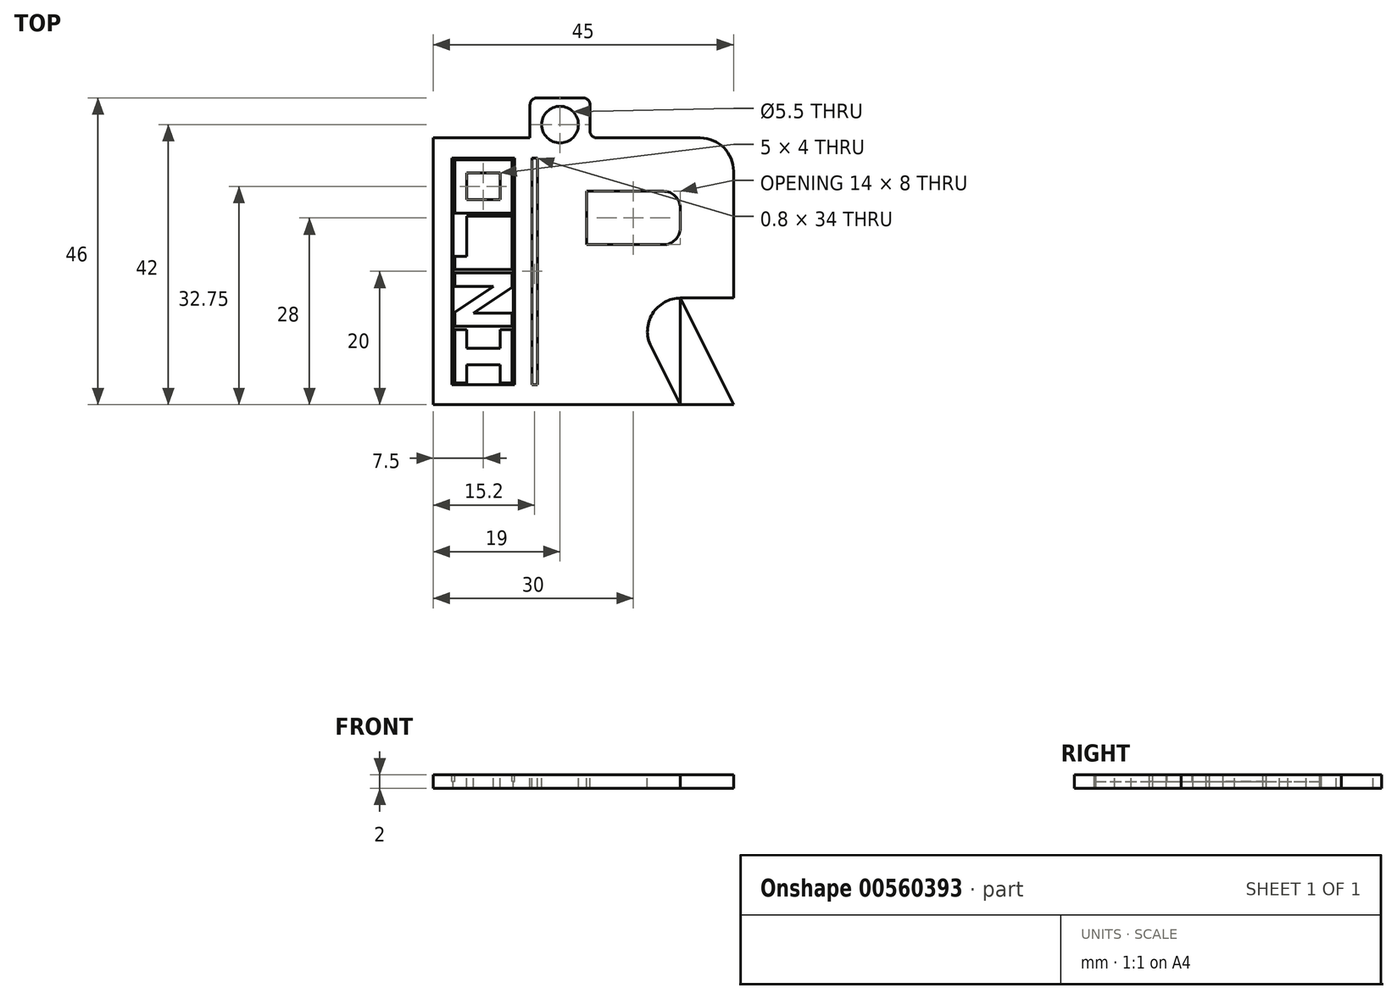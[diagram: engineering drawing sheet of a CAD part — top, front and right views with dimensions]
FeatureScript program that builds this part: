
annotation { "Feature Type Name" : "Feature", "Feature Type Description" : "" }
export const myFeature = defineFeature(function(context is Context, id is Id, definition is map)
    precondition{}
    {
        {
            var Q0;
            Q0=qCreatedBy(makeId("Top.planeOp"),FACE);
            var sketch = newSketch(context, id + "F0", { "sketchPlane" : qUnion([Q0])});
            skPoint(sketch, "E0.middle", {"position": v(0, 0) * mm});
            skLineSegment(sketch, "E1.bottom", {"start": v(-15, 20) * mm, "end": v(15, 20) * mm});
            skLineSegment(sketch, "E1.top", {"start": v(-15, -20) * mm, "end": v(15, -20) * mm});
            skLineSegment(sketch, "E1.left", {"start": v(-15, 20) * mm, "end": v(-15, -20) * mm});
            skLineSegment(sketch, "E1.right", {"start": v(15, 20) * mm, "end": v(15, -20) * mm});
            skSolve(sketch);
        }
        {
            var Q0;
            Q0=makeQuery(id+"F0.imprint","IMPRINT",FACE,{"disambiguationData":[TD([[makeQuery(id+"F0.imprint","IMPRINT",EDGE,{"derivedFrom":sQuery(id+"F0.wireOp",EDGE,"E1.bottom")}),-1.0]])]});
            extrude(context, id + "F1", {"entities" : qUnion([Q0]), "depth" : 2 * mm, "offsetDistance" : 25 * mm});
        }
        {
            var Q0;
            Q0=makeQuery(id+"F1.opExtrude","CAP_FACE",FACE,{"disambiguationData":[OSD([sQuery(id+"F0.wireOp",EDGE,"E1.bottom"),sQuery(id+"F0.wireOp",EDGE,"E1.top"),sQuery(id+"F0.wireOp",EDGE,"E1.left"),sQuery(id+"F0.wireOp",EDGE,"E1.right")])],"isStart":false});
            var sketch = newSketch(context, id + "F2", { "sketchPlane" : qUnion([Q0])});
            skLineSegment(sketch, "E2.bottom", {"start": v(-7, 12) * mm, "end": v(7, 12) * mm});
            skLineSegment(sketch, "E2.top", {"start": v(-7, 4) * mm, "end": v(7, 4) * mm});
            skLineSegment(sketch, "E2.left", {"start": v(-7, 12) * mm, "end": v(-7, 4) * mm});
            skLineSegment(sketch, "E2.right", {"start": v(7, 12) * mm, "end": v(7, 4) * mm});
            skSolve(sketch);
        }
        {
            var Q0;
            Q0=makeQuery(id+"F2.imprint","IMPRINT",FACE,{"disambiguationData":[TD([[makeQuery(id+"F2.imprint","IMPRINT",EDGE,{"derivedFrom":sQuery(id+"F2.wireOp",EDGE,"E2.bottom")}),-1.0]])]});
            extrude(context, id + "F3", {"entities" : qUnion([Q0]), "operationType" : NewBodyOperationType.REMOVE, "oppositeDirection" : true, "depth" : 10 * mm, "offsetDistance" : 25 * mm});
        }
        {
            var Q0;
            Q0=makeQuery(id+"F1.opExtrude","CAP_FACE",FACE,{"disambiguationData":[OSD([sQuery(id+"F0.wireOp",EDGE,"E1.bottom"),sQuery(id+"F0.wireOp",EDGE,"E1.top"),sQuery(id+"F0.wireOp",EDGE,"E1.left"),sQuery(id+"F0.wireOp",EDGE,"E1.right")])],"isStart":false});
            var sketch = newSketch(context, id + "F4", { "sketchPlane" : qUnion([Q0])});
            skLineSegment(sketch, "E3.bottom", {"start": v(-7, -4) * mm, "end": v(7, -4) * mm});
            skLineSegment(sketch, "E3.top", {"start": v(-7, -20) * mm, "end": v(7, -20) * mm});
            skLineSegment(sketch, "E3.left", {"start": v(-7, -4) * mm, "end": v(-7, -20) * mm});
            skLineSegment(sketch, "E3.right", {"start": v(7, -4) * mm, "end": v(7, -20) * mm});
            skLineSegment(sketch, "E4", {"start": v(-1, -4) * mm, "end": v(7, -20) * mm});
            skLineSegment(sketch, "E5", {"start": v(-1, -4) * mm, "end": v(7, -4) * mm});
            skLineSegment(sketch, "E6", {"start": v(7, -4) * mm, "end": v(15, -20) * mm});
            skLineSegment(sketch, "E7", {"start": v(15, -20) * mm, "end": v(7, -20) * mm});
            skLineSegment(sketch, "E8", {"start": v(7, -4) * mm, "end": v(15, -4) * mm});
            skSolve(sketch);
        }
        {
            var Q0;
            Q0=makeQuery(id+"F4.imprint","IMPRINT",FACE,{"disambiguationData":[TD([[makeQuery(id+"F4.imprint","IMPRINT",EDGE,{"derivedFrom":sQuery(id+"F4.wireOp",EDGE,"E3.bottom")}),-1.0]])]});
            var Q1;
            {var subQ0=sQuery(id+"F4.wireOp",EDGE,"E6");Q1=makeQuery(id+"F4.imprint","IMPRINT",FACE,{"disambiguationData":[TD([[makeQuery(id+"F4.imprint","IMPRINT",EDGE,{"derivedFrom":subQ0}),1.0]])]});}
            extrude(context, id + "F5", {"entities" : qUnion([Q0, Q1]), "operationType" : NewBodyOperationType.REMOVE, "oppositeDirection" : true, "depth" : 10 * mm, "offsetDistance" : 25 * mm});
        }
        {
            var Q0;
            Q0=makeQuery(id+"F5.boolean.opBoolean","COPY",EDGE,{"derivedFrom":makeQuery(id+"F5.opExtrude","SWEPT_EDGE",EDGE,{"disambiguationData":[OSD([sQuery(id+"F0.wireOp",EDGE,"E1.right"),sQuery(id+"F4.wireOp",EDGE,"E8")])]})});
            var Q1;
            Q1=makeQuery(id+"F1.opExtrude","SWEPT_EDGE",EDGE,{"disambiguationData":[OSD([sQuery(id+"F0.wireOp",EDGE,"E1.bottom"),sQuery(id+"F0.wireOp",EDGE,"E1.right")])]});
            var Q2;
            Q2=makeQuery(id+"F5.boolean.opBoolean","COPY",EDGE,{"derivedFrom":makeQuery(id+"F5.opExtrude","SWEPT_EDGE",EDGE,{"disambiguationData":[OSD([sQuery(id+"F4.wireOp",EDGE,"E3.bottom"),sQuery(id+"F4.wireOp",EDGE,"E4"),sQuery(id+"F4.wireOp",EDGE,"E5")])]})});
            fillet(context, id + "F6", {"entities" : qUnion([Q0, Q1, Q2]), "radius" : 5 * mm, "tangentPropagation" : true, "allowEdgeOverflow" : false});
        }
        {
            var Q0;
            Q0=makeQuery(id+"F3.boolean.opBoolean","COPY",EDGE,{"derivedFrom":makeQuery(id+"F3.opExtrude","SWEPT_EDGE",EDGE,{"disambiguationData":[OSD([sQuery(id+"F2.wireOp",EDGE,"E2.bottom"),sQuery(id+"F2.wireOp",EDGE,"E2.right")])]})});
            var Q1;
            Q1=makeQuery(id+"F3.boolean.opBoolean","COPY",EDGE,{"derivedFrom":makeQuery(id+"F3.opExtrude","SWEPT_EDGE",EDGE,{"disambiguationData":[OSD([sQuery(id+"F2.wireOp",EDGE,"E2.top"),sQuery(id+"F2.wireOp",EDGE,"E2.right")])]})});
            fillet(context, id + "F7", {"entities" : qUnion([Q0, Q1]), "radius" : 2.5 * mm, "tangentPropagation" : true, "allowEdgeOverflow" : false});
        }
        {
            var Q0;
            Q0=makeQuery(id+"F1.opExtrude","CAP_FACE",FACE,{"disambiguationData":[OSD([sQuery(id+"F0.wireOp",EDGE,"E1.bottom"),sQuery(id+"F0.wireOp",EDGE,"E1.top"),sQuery(id+"F0.wireOp",EDGE,"E1.left"),sQuery(id+"F0.wireOp",EDGE,"E1.right")])],"isStart":false});
            var sketch = newSketch(context, id + "F8", { "sketchPlane" : qUnion([Q0])});
            skLineSegment(sketch, "E9.bottom", {"start": v(-15, 20) * mm, "end": v(-30, 20) * mm});
            skLineSegment(sketch, "E9.top", {"start": v(-15, -20) * mm, "end": v(-30, -20) * mm});
            skLineSegment(sketch, "E9.left", {"start": v(-15, 20) * mm, "end": v(-15, -20) * mm});
            skLineSegment(sketch, "E9.right", {"start": v(-30, 20) * mm, "end": v(-30, -20) * mm});
            skLineSegment(sketch, "E10.bottom", {"start": v(-27, 17) * mm, "end": v(-18, 17) * mm});
            skLineSegment(sketch, "E10.top", {"start": v(-27, -17) * mm, "end": v(-18, -17) * mm});
            skLineSegment(sketch, "E10.left", {"start": v(-27, 17) * mm, "end": v(-27, -17) * mm});
            skLineSegment(sketch, "E10.right", {"start": v(-18, 17) * mm, "end": v(-18, -17) * mm});
            skSolve(sketch);
        }
        {
            var Q0;
            Q0=makeQuery(id+"F8.imprint","IMPRINT",FACE,{"disambiguationData":[TD([[makeQuery(id+"F8.imprint","IMPRINT",EDGE,{"derivedFrom":sQuery(id+"F8.wireOp",EDGE,"E9.bottom")}),1.0]])]});
            extrude(context, id + "F9", {"entities" : qUnion([Q0]), "operationType" : NewBodyOperationType.ADD, "oppositeDirection" : true, "depth" : 2 * mm, "offsetDistance" : 25 * mm});
        }
        {
            var Q0;
            Q0=makeQuery(id+"F9.boolean.opBoolean","MERGE",FACE,{"derivedFrom":[makeQuery(id+"F1.opExtrude","CAP_FACE",FACE,{"disambiguationData":[OSD([sQuery(id+"F0.wireOp",EDGE,"E1.bottom"),sQuery(id+"F0.wireOp",EDGE,"E1.top"),sQuery(id+"F0.wireOp",EDGE,"E1.left"),sQuery(id+"F0.wireOp",EDGE,"E1.right")])],"isStart":false}),makeQuery(id+"F9.opExtrude","CAP_FACE",FACE,{"disambiguationData":[OSD([sQuery(id+"F8.wireOp",EDGE,"E9.bottom"),sQuery(id+"F8.wireOp",EDGE,"E9.top"),sQuery(id+"F8.wireOp",EDGE,"E9.left"),sQuery(id+"F8.wireOp",EDGE,"E9.right"),sQuery(id+"F8.wireOp",EDGE,"E10.bottom"),sQuery(id+"F8.wireOp",EDGE,"E10.top"),sQuery(id+"F8.wireOp",EDGE,"E10.left"),sQuery(id+"F8.wireOp",EDGE,"E10.right")])],"isStart":true})]});
            var sketch = newSketch(context, id + "F10", { "sketchPlane" : qUnion([Q0])});
            skLineSegment(sketch, "E11.bottom", {"start": v(-15.2, 17) * mm, "end": v(-14.4, 17) * mm});
            skLineSegment(sketch, "E11.top", {"start": v(-15.2, -17) * mm, "end": v(-14.4, -17) * mm});
            skLineSegment(sketch, "E11.left", {"start": v(-15.2, 17) * mm, "end": v(-15.2, -17) * mm});
            skLineSegment(sketch, "E11.right", {"start": v(-14.4, 17) * mm, "end": v(-14.4, -17) * mm});
            skSolve(sketch);
        }
        {
            var Q0;
            Q0=makeQuery(id+"F10.imprint","IMPRINT",FACE,{"disambiguationData":[TD([[makeQuery(id+"F10.imprint","IMPRINT",EDGE,{"derivedFrom":sQuery(id+"F10.wireOp",EDGE,"E11.bottom")}),-1.0]])]});
            extrude(context, id + "F11", {"entities" : qUnion([Q0]), "operationType" : NewBodyOperationType.REMOVE, "oppositeDirection" : true, "depth" : 10 * mm, "offsetDistance" : 25 * mm});
        }
        {
            var Q0;
            Q0=makeQuery(id+"F9.boolean.opBoolean","MERGE",FACE,{"derivedFrom":[makeQuery(id+"F1.opExtrude","CAP_FACE",FACE,{"disambiguationData":[OSD([sQuery(id+"F0.wireOp",EDGE,"E1.bottom"),sQuery(id+"F0.wireOp",EDGE,"E1.top"),sQuery(id+"F0.wireOp",EDGE,"E1.left"),sQuery(id+"F0.wireOp",EDGE,"E1.right")])],"isStart":false}),makeQuery(id+"F9.opExtrude","CAP_FACE",FACE,{"disambiguationData":[OSD([sQuery(id+"F8.wireOp",EDGE,"E9.bottom"),sQuery(id+"F8.wireOp",EDGE,"E9.top"),sQuery(id+"F8.wireOp",EDGE,"E9.left"),sQuery(id+"F8.wireOp",EDGE,"E9.right"),sQuery(id+"F8.wireOp",EDGE,"E10.bottom"),sQuery(id+"F8.wireOp",EDGE,"E10.top"),sQuery(id+"F8.wireOp",EDGE,"E10.left"),sQuery(id+"F8.wireOp",EDGE,"E10.right")])],"isStart":true})]});
            var sketch = newSketch(context, id + "F12", { "sketchPlane" : qUnion([Q0])});
            skLineSegment(sketch, "E12.bottom", {"start": v(-27, 17) * mm, "end": v(-18, 17) * mm});
            skLineSegment(sketch, "E12.top", {"start": v(-27, -17) * mm, "end": v(-18, -17) * mm});
            skLineSegment(sketch, "E12.left", {"start": v(-27, 17) * mm, "end": v(-27, -17) * mm});
            skLineSegment(sketch, "E13", {"start": v(-18, -17) * mm, "end": v(-18, -16.75) * mm});
            skLineSegment(sketch, "E14", {"start": v(-18, -16.75) * mm, "end": v(-18, -8.75) * mm});
            skLineSegment(sketch, "E15", {"start": v(-18, -8.75) * mm, "end": v(-18, -8.25) * mm});
            skLineSegment(sketch, "E16", {"start": v(-18, -8.25) * mm, "end": v(-18, -0.25) * mm});
            skLineSegment(sketch, "E17", {"start": v(-18, -0.25) * mm, "end": v(-18, 0.25) * mm});
            skLineSegment(sketch, "E18", {"start": v(-18, 0.25) * mm, "end": v(-18, 8.25) * mm});
            skLineSegment(sketch, "E19", {"start": v(-18, 8.25) * mm, "end": v(-18, 8.75) * mm});
            skLineSegment(sketch, "E20", {"start": v(-18, 8.75) * mm, "end": v(-18, 16.75) * mm});
            skLineSegment(sketch, "E21", {"start": v(-18, 16.75) * mm, "end": v(-18, 17) * mm});
            skLineSegment(sketch, "E22.bottom", {"start": v(-18, -16.75) * mm, "end": v(-27, -16.75) * mm});
            skLineSegment(sketch, "E22.top", {"start": v(-18, -8.75) * mm, "end": v(-27, -8.75) * mm});
            skLineSegment(sketch, "E22.right", {"start": v(-27, -16.75) * mm, "end": v(-27, -8.75) * mm});
            skLineSegment(sketch, "E23.bottom", {"start": v(-18, -8.25) * mm, "end": v(-27, -8.25) * mm});
            skLineSegment(sketch, "E23.top", {"start": v(-18, -0.25) * mm, "end": v(-27, -0.25) * mm});
            skLineSegment(sketch, "E23.right", {"start": v(-27, -8.25) * mm, "end": v(-27, -0.25) * mm});
            skLineSegment(sketch, "E24.bottom", {"start": v(-18, 0.25) * mm, "end": v(-27, 0.25) * mm});
            skLineSegment(sketch, "E24.top", {"start": v(-18, 8.25) * mm, "end": v(-27, 8.25) * mm});
            skLineSegment(sketch, "E24.right", {"start": v(-27, 0.25) * mm, "end": v(-27, 8.25) * mm});
            skLineSegment(sketch, "E25.bottom", {"start": v(-18, 8.75) * mm, "end": v(-27, 8.75) * mm});
            skLineSegment(sketch, "E25.top", {"start": v(-18, 16.75) * mm, "end": v(-27, 16.75) * mm});
            skLineSegment(sketch, "E25.right", {"start": v(-27, 8.75) * mm, "end": v(-27, 16.75) * mm});
            skSolve(sketch);
        }
        {
            var Q0;
            Q0=makeQuery(id+"F12.imprint","IMPRINT",FACE,{"disambiguationData":[TD([[makeQuery(id+"F12.imprint","IMPRINT",EDGE,{"derivedFrom":sQuery(id+"F12.wireOp",EDGE,"E22.bottom")}),-1.0]])]});
            var Q1;
            Q1=makeQuery(id+"F12.imprint","IMPRINT",FACE,{"disambiguationData":[TD([[makeQuery(id+"F12.imprint","IMPRINT",EDGE,{"derivedFrom":sQuery(id+"F12.wireOp",EDGE,"E23.bottom")}),-1.0]])]});
            var Q2;
            Q2=makeQuery(id+"F12.imprint","IMPRINT",FACE,{"disambiguationData":[TD([[makeQuery(id+"F12.imprint","IMPRINT",EDGE,{"derivedFrom":sQuery(id+"F12.wireOp",EDGE,"E24.bottom")}),-1.0]])]});
            var Q3;
            Q3=makeQuery(id+"F12.imprint","IMPRINT",FACE,{"disambiguationData":[TD([[makeQuery(id+"F12.imprint","IMPRINT",EDGE,{"derivedFrom":sQuery(id+"F12.wireOp",EDGE,"E25.bottom")}),-1.0]])]});
            extrude(context, id + "F13", {"entities" : qUnion([Q0, Q1, Q2, Q3]), "operationType" : NewBodyOperationType.ADD, "oppositeDirection" : true, "depth" : 2 * mm, "offsetDistance" : 25 * mm});
        }
        {
            var Q0;
            Q0=makeQuery(id+"F13.boolean.opBoolean","MERGE",FACE,{"derivedFrom":[makeQuery(id+"F9.boolean.opBoolean","MERGE",FACE,{"derivedFrom":[makeQuery(id+"F1.opExtrude","CAP_FACE",FACE,{"disambiguationData":[OSD([sQuery(id+"F0.wireOp",EDGE,"E1.bottom"),sQuery(id+"F0.wireOp",EDGE,"E1.top"),sQuery(id+"F0.wireOp",EDGE,"E1.left"),sQuery(id+"F0.wireOp",EDGE,"E1.right")])],"isStart":false}),makeQuery(id+"F9.opExtrude","CAP_FACE",FACE,{"disambiguationData":[OSD([sQuery(id+"F8.wireOp",EDGE,"E9.bottom"),sQuery(id+"F8.wireOp",EDGE,"E9.top"),sQuery(id+"F8.wireOp",EDGE,"E9.left"),sQuery(id+"F8.wireOp",EDGE,"E9.right"),sQuery(id+"F8.wireOp",EDGE,"E10.bottom"),sQuery(id+"F8.wireOp",EDGE,"E10.top"),sQuery(id+"F8.wireOp",EDGE,"E10.left"),sQuery(id+"F8.wireOp",EDGE,"E10.right")])],"isStart":true})]}),makeQuery(id+"F13.opExtrude","CAP_FACE",FACE,{"disambiguationData":[OSD([sQuery(id+"F12.wireOp",EDGE,"E22.bottom"),sQuery(id+"F12.wireOp",EDGE,"E22.top"),sQuery(id+"F12.wireOp",EDGE,"E14"),sQuery(id+"F12.wireOp",EDGE,"E22.right")])],"isStart":true}),makeQuery(id+"F13.opExtrude","CAP_FACE",FACE,{"disambiguationData":[OSD([sQuery(id+"F12.wireOp",EDGE,"E23.bottom"),sQuery(id+"F12.wireOp",EDGE,"E23.top"),sQuery(id+"F12.wireOp",EDGE,"E16"),sQuery(id+"F12.wireOp",EDGE,"E23.right")])],"isStart":true}),makeQuery(id+"F13.opExtrude","CAP_FACE",FACE,{"disambiguationData":[OSD([sQuery(id+"F12.wireOp",EDGE,"E24.bottom"),sQuery(id+"F12.wireOp",EDGE,"E24.top"),sQuery(id+"F12.wireOp",EDGE,"E18"),sQuery(id+"F12.wireOp",EDGE,"E24.right")])],"isStart":true}),makeQuery(id+"F13.opExtrude","CAP_FACE",FACE,{"disambiguationData":[OSD([sQuery(id+"F12.wireOp",EDGE,"E25.bottom"),sQuery(id+"F12.wireOp",EDGE,"E25.top"),sQuery(id+"F12.wireOp",EDGE,"E20"),sQuery(id+"F12.wireOp",EDGE,"E25.right")])],"isStart":true})]});
            var sketch = newSketch(context, id + "F14", { "sketchPlane" : qUnion([Q0])});
            skLineSegment(sketch, "E26.bottom", {"start": v(-27, -16.75) * mm, "end": v(-18, -16.75) * mm});
            skLineSegment(sketch, "E26.top", {"start": v(-27, -8.75) * mm, "end": v(-18, -8.75) * mm});
            skLineSegment(sketch, "E26.left", {"start": v(-27, -16.75) * mm, "end": v(-27, -8.75) * mm});
            skLineSegment(sketch, "E26.right", {"start": v(-18, -16.75) * mm, "end": v(-18, -8.75) * mm});
            skLineSegment(sketch, "E27.bottom", {"start": v(-27, -8.25) * mm, "end": v(-18, -8.25) * mm});
            skLineSegment(sketch, "E27.top", {"start": v(-27, -0.25) * mm, "end": v(-18, -0.25) * mm});
            skLineSegment(sketch, "E27.left", {"start": v(-27, -8.25) * mm, "end": v(-27, -0.25) * mm});
            skLineSegment(sketch, "E27.right", {"start": v(-18, -8.25) * mm, "end": v(-18, -0.25) * mm});
            skLineSegment(sketch, "E28.bottom", {"start": v(-27, 0.25) * mm, "end": v(-18, 0.25) * mm});
            skLineSegment(sketch, "E28.top", {"start": v(-27, 8.25) * mm, "end": v(-18, 8.25) * mm});
            skLineSegment(sketch, "E28.left", {"start": v(-27, 0.25) * mm, "end": v(-27, 8.25) * mm});
            skLineSegment(sketch, "E28.right", {"start": v(-18, 0.25) * mm, "end": v(-18, 8.25) * mm});
            skLineSegment(sketch, "E29.bottom", {"start": v(-27, 8.75) * mm, "end": v(-18, 8.75) * mm});
            skLineSegment(sketch, "E29.top", {"start": v(-27, 16.75) * mm, "end": v(-18, 16.75) * mm});
            skLineSegment(sketch, "E29.left", {"start": v(-27, 8.75) * mm, "end": v(-27, 16.75) * mm});
            skLineSegment(sketch, "E29.right", {"start": v(-18, 8.75) * mm, "end": v(-18, 16.75) * mm});
            skLineSegment(sketch, "E30.bottom", {"start": v(-18, -16.75) * mm, "end": v(-20, -16.75) * mm});
            skLineSegment(sketch, "E30.top", {"start": v(-18, -8.75) * mm, "end": v(-20, -8.75) * mm});
            skLineSegment(sketch, "E30.right", {"start": v(-20, -16.75) * mm, "end": v(-20, -8.75) * mm});
            skLineSegment(sketch, "E31.bottom", {"start": v(-27, -16.75) * mm, "end": v(-25, -16.75) * mm});
            skLineSegment(sketch, "E31.top", {"start": v(-27, -8.75) * mm, "end": v(-25, -8.75) * mm});
            skLineSegment(sketch, "E31.right", {"start": v(-25, -16.75) * mm, "end": v(-25, -8.75) * mm});
            skLineSegment(sketch, "E32.bottom", {"start": v(-25, -14) * mm, "end": v(-20, -14) * mm});
            skLineSegment(sketch, "E32.top", {"start": v(-25, -11.5) * mm, "end": v(-20, -11.5) * mm});
            skLineSegment(sketch, "E32.left", {"start": v(-25, -14) * mm, "end": v(-25, -11.5) * mm});
            skLineSegment(sketch, "E32.right", {"start": v(-20, -14) * mm, "end": v(-20, -11.5) * mm});
            skLineSegment(sketch, "E33.bottom", {"start": v(-27, -6.25) * mm, "end": v(-18, -6.25) * mm});
            skLineSegment(sketch, "E33.top", {"start": v(-27, -2.25) * mm, "end": v(-18, -2.25) * mm});
            skLineSegment(sketch, "E33.left", {"start": v(-27, -6.25) * mm, "end": v(-27, -2.25) * mm});
            skLineSegment(sketch, "E33.right", {"start": v(-18, -6.25) * mm, "end": v(-18, -2.25) * mm});
            skLineSegment(sketch, "E34", {"start": v(-18, -2.25) * mm, "end": v(-21, -2.25) * mm});
            skLineSegment(sketch, "E35", {"start": v(-21, -2.25) * mm, "end": v(-27, -6.25) * mm});
            skLineSegment(sketch, "E36", {"start": v(-27, -6.25) * mm, "end": v(-24, -6.25) * mm});
            skLineSegment(sketch, "E37", {"start": v(-24, -6.25) * mm, "end": v(-18, -2.25) * mm});
            skLineSegment(sketch, "E38.bottom", {"start": v(-18, 0.25) * mm, "end": v(-27, 0.25) * mm});
            skLineSegment(sketch, "E38.top", {"start": v(-18, 2.25) * mm, "end": v(-27, 2.25) * mm});
            skLineSegment(sketch, "E38.left", {"start": v(-18, 0.25) * mm, "end": v(-18, 2.25) * mm});
            skLineSegment(sketch, "E38.right", {"start": v(-27, 0.25) * mm, "end": v(-27, 2.25) * mm});
            skLineSegment(sketch, "E39.bottom", {"start": v(-27, 2.25) * mm, "end": v(-25, 2.25) * mm});
            skLineSegment(sketch, "E39.top", {"start": v(-27, 8.25) * mm, "end": v(-25, 8.25) * mm});
            skLineSegment(sketch, "E39.left", {"start": v(-27, 2.25) * mm, "end": v(-27, 8.25) * mm});
            skLineSegment(sketch, "E39.right", {"start": v(-25, 2.25) * mm, "end": v(-25, 8.25) * mm});
            skLineSegment(sketch, "E40.bottom", {"start": v(-23.5, 2.25) * mm, "end": v(-21.5, 2.25) * mm});
            skLineSegment(sketch, "E40.top", {"start": v(-23.5, 7.25) * mm, "end": v(-21.5, 7.25) * mm});
            skLineSegment(sketch, "E40.left", {"start": v(-23.5, 2.25) * mm, "end": v(-23.5, 7.25) * mm});
            skLineSegment(sketch, "E40.right", {"start": v(-21.5, 2.25) * mm, "end": v(-21.5, 7.25) * mm});
            skLineSegment(sketch, "E41.bottom", {"start": v(-25, 10.75) * mm, "end": v(-20, 10.75) * mm});
            skLineSegment(sketch, "E41.top", {"start": v(-25, 14.75) * mm, "end": v(-20, 14.75) * mm});
            skLineSegment(sketch, "E41.left", {"start": v(-25, 10.75) * mm, "end": v(-25, 14.75) * mm});
            skLineSegment(sketch, "E41.right", {"start": v(-20, 10.75) * mm, "end": v(-20, 14.75) * mm});
            skSolve(sketch);
        }
        {
            var Q0;
            {var subQ0=sQuery(id+"F14.wireOp",EDGE,"E26.bottom");Q0=makeQuery(id+"F14.imprint","IMPRINT",FACE,{"disambiguationData":[TD([[makeQuery(id+"F14.imprint","IMPRINT",EDGE,{"derivedFrom":subQ0}),-1.0]])]});}
            var Q1;
            {var subQ0=sQuery(id+"F14.wireOp",EDGE,"E26.top");Q1=makeQuery(id+"F14.imprint","IMPRINT",FACE,{"disambiguationData":[TD([[makeQuery(id+"F14.imprint","IMPRINT",EDGE,{"derivedFrom":subQ0}),1.0]])]});}
            var Q2;
            Q2=makeQuery(id+"F14.imprint","IMPRINT",FACE,{"disambiguationData":[TD([[makeQuery(id+"F14.imprint","IMPRINT",EDGE,{"derivedFrom":sQuery(id+"F14.wireOp",EDGE,"E33.top")}),-1.0]])]});
            var Q3;
            Q3=makeQuery(id+"F14.imprint","IMPRINT",FACE,{"disambiguationData":[TD([[makeQuery(id+"F14.imprint","IMPRINT",EDGE,{"derivedFrom":sQuery(id+"F14.wireOp",EDGE,"E33.bottom")}),1.0]])]});
            var Q4;
            Q4=makeQuery(id+"F14.imprint","IMPRINT",FACE,{"disambiguationData":[TD([[makeQuery(id+"F14.imprint","IMPRINT",EDGE,{"derivedFrom":sQuery(id+"F14.wireOp",EDGE,"E28.top")}),1.0]])]});
            var Q5;
            Q5=makeQuery(id+"F14.imprint","IMPRINT",FACE,{"disambiguationData":[TD([[makeQuery(id+"F14.imprint","IMPRINT",EDGE,{"derivedFrom":sQuery(id+"F14.wireOp",EDGE,"E41.bottom")}),1.0]])]});
            extrude(context, id + "F15", {"entities" : qUnion([Q0, Q1, Q2, Q3, Q4, Q5]), "operationType" : NewBodyOperationType.REMOVE, "oppositeDirection" : true, "depth" : 10 * mm, "offsetDistance" : 25 * mm});
        }
        {
            var Q0;
            Q0=makeQuery(id+"F13.boolean.opBoolean","MERGE",FACE,{"derivedFrom":[makeQuery(id+"F9.boolean.opBoolean","MERGE",FACE,{"derivedFrom":[makeQuery(id+"F1.opExtrude","CAP_FACE",FACE,{"disambiguationData":[OSD([sQuery(id+"F0.wireOp",EDGE,"E1.bottom"),sQuery(id+"F0.wireOp",EDGE,"E1.top"),sQuery(id+"F0.wireOp",EDGE,"E1.left"),sQuery(id+"F0.wireOp",EDGE,"E1.right")])],"isStart":false}),makeQuery(id+"F9.opExtrude","CAP_FACE",FACE,{"disambiguationData":[OSD([sQuery(id+"F8.wireOp",EDGE,"E9.bottom"),sQuery(id+"F8.wireOp",EDGE,"E9.top"),sQuery(id+"F8.wireOp",EDGE,"E9.left"),sQuery(id+"F8.wireOp",EDGE,"E9.right"),sQuery(id+"F8.wireOp",EDGE,"E10.bottom"),sQuery(id+"F8.wireOp",EDGE,"E10.top"),sQuery(id+"F8.wireOp",EDGE,"E10.left"),sQuery(id+"F8.wireOp",EDGE,"E10.right")])],"isStart":true})]}),makeQuery(id+"F13.opExtrude","CAP_FACE",FACE,{"disambiguationData":[OSD([sQuery(id+"F12.wireOp",EDGE,"E22.bottom"),sQuery(id+"F12.wireOp",EDGE,"E22.top"),sQuery(id+"F12.wireOp",EDGE,"E14"),sQuery(id+"F12.wireOp",EDGE,"E22.right")])],"isStart":true}),makeQuery(id+"F13.opExtrude","CAP_FACE",FACE,{"disambiguationData":[OSD([sQuery(id+"F12.wireOp",EDGE,"E23.bottom"),sQuery(id+"F12.wireOp",EDGE,"E23.top"),sQuery(id+"F12.wireOp",EDGE,"E16"),sQuery(id+"F12.wireOp",EDGE,"E23.right")])],"isStart":true}),makeQuery(id+"F13.opExtrude","CAP_FACE",FACE,{"disambiguationData":[OSD([sQuery(id+"F12.wireOp",EDGE,"E24.bottom"),sQuery(id+"F12.wireOp",EDGE,"E24.top"),sQuery(id+"F12.wireOp",EDGE,"E18"),sQuery(id+"F12.wireOp",EDGE,"E24.right")])],"isStart":true}),makeQuery(id+"F13.opExtrude","CAP_FACE",FACE,{"disambiguationData":[OSD([sQuery(id+"F12.wireOp",EDGE,"E25.bottom"),sQuery(id+"F12.wireOp",EDGE,"E25.top"),sQuery(id+"F12.wireOp",EDGE,"E20"),sQuery(id+"F12.wireOp",EDGE,"E25.right")])],"isStart":true})]});
            var sketch = newSketch(context, id + "F16", { "sketchPlane" : qUnion([Q0])});
            skLineSegment(sketch, "E42.bottom", {"start": v(-27.2, -17) * mm, "end": v(-26.8, -17) * mm});
            skLineSegment(sketch, "E42.top", {"start": v(-27.2, 17) * mm, "end": v(-26.8, 17) * mm});
            skLineSegment(sketch, "E42.left", {"start": v(-27.2, -17) * mm, "end": v(-27.2, 17) * mm});
            skLineSegment(sketch, "E42.right", {"start": v(-26.8, -17) * mm, "end": v(-26.8, 17) * mm});
            skLineSegment(sketch, "E43.bottom", {"start": v(-18.2, -17) * mm, "end": v(-17.8, -17) * mm});
            skLineSegment(sketch, "E43.top", {"start": v(-18.2, 17) * mm, "end": v(-17.8, 17) * mm});
            skLineSegment(sketch, "E43.left", {"start": v(-18.2, -17) * mm, "end": v(-18.2, 17) * mm});
            skLineSegment(sketch, "E43.right", {"start": v(-17.8, -17) * mm, "end": v(-17.8, 17) * mm});
            skSolve(sketch);
        }
        {
            var Q0;
            {var subQ30=sQuery(id+"F16.wireOp",EDGE,"E42.left");Q0=makeQuery(id+"F16.imprint","IMPRINT",FACE,{"disambiguationData":[TD([[makeQuery(id+"F16.imprint","IMPRINT",EDGE,{"derivedFrom":subQ30}),-1.0]])]});}
            var Q1;
            {var subQ39=sQuery(id+"F16.wireOp",EDGE,"E43.right");Q1=makeQuery(id+"F16.imprint","IMPRINT",FACE,{"disambiguationData":[TD([[makeQuery(id+"F16.imprint","IMPRINT",EDGE,{"derivedFrom":subQ39}),1.0]])]});}
            extrude(context, id + "F17", {"entities" : qUnion([Q0, Q1]), "operationType" : NewBodyOperationType.REMOVE, "oppositeDirection" : true, "depth" : 1 * mm, "offsetDistance" : 25 * mm});
        }
        {
            var Q0;
            {var subQ0=sQuery(id+"F8.wireOp",EDGE,"E10.top");var subQ1=sQuery(id+"F0.wireOp",EDGE,"E1.top");var subQ2=sQuery(id+"F8.wireOp",EDGE,"E10.bottom");var subQ3=sQuery(id+"F8.wireOp",EDGE,"E9.bottom");var subQ8=sQuery(id+"F0.wireOp",EDGE,"E1.right");var subQ9=sQuery(id+"F0.wireOp",EDGE,"E1.bottom");var subQ10=sQuery(id+"F8.wireOp",EDGE,"E9.right");var subQ13=sQuery(id+"F8.wireOp",EDGE,"E9.top");Q0=makeQuery(id+"F17.boolean.opBoolean","SPLIT",FACE,{"disambiguationData":[TD([makeQuery(id+"F1.opExtrude","SWEPT_FACE",FACE,{"disambiguationData":[OSD([subQ9])]})])],"derivedFrom":makeQuery(id+"F13.boolean.opBoolean","MERGE",FACE,{"derivedFrom":[makeQuery(id+"F9.boolean.opBoolean","MERGE",FACE,{"derivedFrom":[makeQuery(id+"F1.opExtrude","CAP_FACE",FACE,{"disambiguationData":[OSD([subQ9,subQ1,sQuery(id+"F0.wireOp",EDGE,"E1.left"),subQ8])],"isStart":false}),makeQuery(id+"F9.opExtrude","CAP_FACE",FACE,{"disambiguationData":[OSD([subQ3,subQ13,sQuery(id+"F8.wireOp",EDGE,"E9.left"),subQ10,subQ2,subQ0,sQuery(id+"F8.wireOp",EDGE,"E10.left"),sQuery(id+"F8.wireOp",EDGE,"E10.right")])],"isStart":true})]}),makeQuery(id+"F13.opExtrude","CAP_FACE",FACE,{"disambiguationData":[OSD([sQuery(id+"F12.wireOp",EDGE,"E22.bottom"),sQuery(id+"F12.wireOp",EDGE,"E22.top"),sQuery(id+"F12.wireOp",EDGE,"E14"),sQuery(id+"F12.wireOp",EDGE,"E22.right")])],"isStart":true}),makeQuery(id+"F13.opExtrude","CAP_FACE",FACE,{"disambiguationData":[OSD([sQuery(id+"F12.wireOp",EDGE,"E23.bottom"),sQuery(id+"F12.wireOp",EDGE,"E23.top"),sQuery(id+"F12.wireOp",EDGE,"E16"),sQuery(id+"F12.wireOp",EDGE,"E23.right")])],"isStart":true}),makeQuery(id+"F13.opExtrude","CAP_FACE",FACE,{"disambiguationData":[OSD([sQuery(id+"F12.wireOp",EDGE,"E24.bottom"),sQuery(id+"F12.wireOp",EDGE,"E24.top"),sQuery(id+"F12.wireOp",EDGE,"E18"),sQuery(id+"F12.wireOp",EDGE,"E24.right")])],"isStart":true}),makeQuery(id+"F13.opExtrude","CAP_FACE",FACE,{"disambiguationData":[OSD([sQuery(id+"F12.wireOp",EDGE,"E25.bottom"),sQuery(id+"F12.wireOp",EDGE,"E25.top"),sQuery(id+"F12.wireOp",EDGE,"E20"),sQuery(id+"F12.wireOp",EDGE,"E25.right")])],"isStart":true})]})});}
            var sketch = newSketch(context, id + "F18", { "sketchPlane" : qUnion([Q0])});
            skLineSegment(sketch, "E44.bottom", {"start": v(-15.5, 20) * mm, "end": v(-6.5, 20) * mm});
            skLineSegment(sketch, "E44.top", {"start": v(-15.5, 26) * mm, "end": v(-6.5, 26) * mm});
            skLineSegment(sketch, "E44.left", {"start": v(-15.5, 20) * mm, "end": v(-15.5, 26) * mm});
            skLineSegment(sketch, "E44.right", {"start": v(-6.5, 20) * mm, "end": v(-6.5, 26) * mm});
            skSolve(sketch);
        }
        {
            var Q0;
            Q0=makeQuery(id+"F18.imprint","IMPRINT",FACE,{"disambiguationData":[TD([[makeQuery(id+"F18.imprint","IMPRINT",EDGE,{"derivedFrom":sQuery(id+"F18.wireOp",EDGE,"E44.bottom")}),1.0]])]});
            extrude(context, id + "F19", {"entities" : qUnion([Q0]), "operationType" : NewBodyOperationType.ADD, "oppositeDirection" : true, "depth" : 2 * mm, "offsetDistance" : 25 * mm});
        }
        {
            var Q0;
            Q0=makeQuery(id+"F19.opExtrude","SWEPT_EDGE",EDGE,{"disambiguationData":[OSD([sQuery(id+"F18.wireOp",EDGE,"E44.top"),sQuery(id+"F18.wireOp",EDGE,"E44.left")])]});
            var Q1;
            Q1=makeQuery(id+"F19.opExtrude","SWEPT_EDGE",EDGE,{"disambiguationData":[OSD([sQuery(id+"F18.wireOp",EDGE,"E44.top"),sQuery(id+"F18.wireOp",EDGE,"E44.right")])]});
            var Q2;
            Q2=makeQuery(id+"F19.opExtrude","SWEPT_EDGE",EDGE,{"disambiguationData":[OSD([sQuery(id+"F0.wireOp",EDGE,"E1.bottom"),sQuery(id+"F8.wireOp",EDGE,"E9.bottom"),sQuery(id+"F18.wireOp",EDGE,"E44.bottom"),sQuery(id+"F18.wireOp",EDGE,"E44.right")])]});
            var Q3;
            Q3=makeQuery(id+"F19.opExtrude","SWEPT_EDGE",EDGE,{"disambiguationData":[OSD([sQuery(id+"F0.wireOp",EDGE,"E1.bottom"),sQuery(id+"F8.wireOp",EDGE,"E9.bottom"),sQuery(id+"F18.wireOp",EDGE,"E44.bottom"),sQuery(id+"F18.wireOp",EDGE,"E44.left")])]});
            fillet(context, id + "F20", {"entities" : qUnion([Q0, Q1, Q2, Q3]), "radius" : 1 * mm, "tangentPropagation" : true, "allowEdgeOverflow" : false});
        }
        {
            var Q0;
            {var subQ0=sQuery(id+"F8.wireOp",EDGE,"E10.top");var subQ1=sQuery(id+"F0.wireOp",EDGE,"E1.top");var subQ2=sQuery(id+"F8.wireOp",EDGE,"E10.bottom");var subQ3=sQuery(id+"F8.wireOp",EDGE,"E9.bottom");var subQ8=sQuery(id+"F0.wireOp",EDGE,"E1.right");var subQ9=sQuery(id+"F0.wireOp",EDGE,"E1.bottom");var subQ10=sQuery(id+"F8.wireOp",EDGE,"E9.right");var subQ13=sQuery(id+"F8.wireOp",EDGE,"E9.top");Q0=makeQuery(id+"F19.boolean.opBoolean","MERGE",FACE,{"derivedFrom":[makeQuery(id+"F17.boolean.opBoolean","SPLIT",FACE,{"disambiguationData":[TD([makeQuery(id+"F1.opExtrude","SWEPT_FACE",FACE,{"disambiguationData":[OSD([subQ9])]})])],"derivedFrom":makeQuery(id+"F13.boolean.opBoolean","MERGE",FACE,{"derivedFrom":[makeQuery(id+"F9.boolean.opBoolean","MERGE",FACE,{"derivedFrom":[makeQuery(id+"F1.opExtrude","CAP_FACE",FACE,{"disambiguationData":[OSD([subQ9,subQ1,sQuery(id+"F0.wireOp",EDGE,"E1.left"),subQ8])],"isStart":false}),makeQuery(id+"F9.opExtrude","CAP_FACE",FACE,{"disambiguationData":[OSD([subQ3,subQ13,sQuery(id+"F8.wireOp",EDGE,"E9.left"),subQ10,subQ2,subQ0,sQuery(id+"F8.wireOp",EDGE,"E10.left"),sQuery(id+"F8.wireOp",EDGE,"E10.right")])],"isStart":true})]}),makeQuery(id+"F13.opExtrude","CAP_FACE",FACE,{"disambiguationData":[OSD([sQuery(id+"F12.wireOp",EDGE,"E22.bottom"),sQuery(id+"F12.wireOp",EDGE,"E22.top"),sQuery(id+"F12.wireOp",EDGE,"E14"),sQuery(id+"F12.wireOp",EDGE,"E22.right")])],"isStart":true}),makeQuery(id+"F13.opExtrude","CAP_FACE",FACE,{"disambiguationData":[OSD([sQuery(id+"F12.wireOp",EDGE,"E23.bottom"),sQuery(id+"F12.wireOp",EDGE,"E23.top"),sQuery(id+"F12.wireOp",EDGE,"E16"),sQuery(id+"F12.wireOp",EDGE,"E23.right")])],"isStart":true}),makeQuery(id+"F13.opExtrude","CAP_FACE",FACE,{"disambiguationData":[OSD([sQuery(id+"F12.wireOp",EDGE,"E24.bottom"),sQuery(id+"F12.wireOp",EDGE,"E24.top"),sQuery(id+"F12.wireOp",EDGE,"E18"),sQuery(id+"F12.wireOp",EDGE,"E24.right")])],"isStart":true}),makeQuery(id+"F13.opExtrude","CAP_FACE",FACE,{"disambiguationData":[OSD([sQuery(id+"F12.wireOp",EDGE,"E25.bottom"),sQuery(id+"F12.wireOp",EDGE,"E25.top"),sQuery(id+"F12.wireOp",EDGE,"E20"),sQuery(id+"F12.wireOp",EDGE,"E25.right")])],"isStart":true})]})}),makeQuery(id+"F19.opExtrude","CAP_FACE",FACE,{"disambiguationData":[OSD([sQuery(id+"F18.wireOp",EDGE,"E44.bottom"),sQuery(id+"F18.wireOp",EDGE,"E44.top"),sQuery(id+"F18.wireOp",EDGE,"E44.left"),sQuery(id+"F18.wireOp",EDGE,"E44.right")])],"isStart":true})]});}
            var sketch = newSketch(context, id + "F21", { "sketchPlane" : qUnion([Q0])});
            skPoint(sketch, "E45", {"position": v(-11, 22) * mm});
            skSolve(sketch);
        }
        {
            var Q0;
            Q0=sQuery(id+"F21.wireOp",VERTEX,"E45");
            var Q1;
            Q1=makeQuery(id+"F1.opExtrude","SWEPT_BODY",BODY,{"disambiguationData":[OSD([sQuery(id+"F0.wireOp",EDGE,"E1.bottom"),sQuery(id+"F0.wireOp",EDGE,"E1.top"),sQuery(id+"F0.wireOp",EDGE,"E1.left"),sQuery(id+"F0.wireOp",EDGE,"E1.right")])]});
            hole(context, id + "F22", {"style" : HoleStyle.C_BORE, "endStyle" : HoleEndStyle.THROUGH, "holeDiameter" : 5.5 * mm, "cBoreDiameter" : 6.5 * mm, "cBoreDepth" : 0 * mm, "isTappedThrough" : true, "tappedDepth" : 12 * mm, "tapClearance" : 3, "locations" : qUnion([Q0]), "scope" : qUnion([Q1])});
        }
    });
